# Revit family: Toilet-Elongated-American_Standard-Cadet_3_FloWise-3075000.020_Series
name_source: partatom
category: Plumbing Fixtures
units: mm (PartAtom-declared; Revit-internal decimal feet)

## family parameters
Always vertical = No
Cut with Voids When Loaded = No
OmniClass Number = 23.45.05.21.11
OmniClass Title = Water Closets
Part Type = Normal
Room Calculation Point = No
Round Connector Dimension = Use Radius
Shared = Yes
Work Plane-Based = Yes

## types (2) — shared parameters
3075.000 Right Height® Elongated Bowl with Seat = No
4000.101 Tank = No
4000.813 Tank with right hand trip lever = No
5024A.65G Preferred Seat Transitional Elongated Luxury Seat = No
ADA Compliant = Yes
Assembly Code = D2010110
Bowl Shape = Elongated
CW Connection = Yes
CWFU = 10
Cold Water Connection Diameter = 1/2"
Cold Water Connection Height = 5 1/2"
Cold Water Connection Width = 2 1/4"
Compliance Certifications = Meets or Exceeds the Following Specifications: • ASME A112.19.2/CSA B45.1-08 for Vitreous China Fixtures • US EPA WaterSense® Specification for HET's
Default Elevation = 0"
Description = Cadet® 3 FloWise® Skirted Chair Height Elongated Bowl With Seat
Finish = Vitreous China-American Standard-020-White
Finish - Trip Lever = Metal-American Standard-Chrome
Flush Rate = (4.8 Lpf/1.28 gpf)
HW Connection = No
Height = 30 3/4"
Inlet Position 1 = Yes
Inlet Position 2 = No
Inlet Position Distance = 2 1/4"
Installation Type = Floor Mounted
Length = 30 1/4"
Manufacturer = American Standard
Material = Vitreous China-American Standard-White
Model = 3075000.020
Product Documentation Link = https://lixil.cdn.celum.cloud
Product Page URL = https://www.americanstandard-us.com
Seat Height = 16 1/2"
URL = http://www.americanstandard-us.com
Vent Connection = No
WFU = 10
Warranty Information = Lifetime warranty on chinaware, 5 year warranty on all mechanical parts, and 1 year warranty on seat
Waste Connection = Yes
Waste Connection Diameter = 2 1/8"
Width = 15 3/4"
zero-valued in all types: HWFU

## per-type parameters (varying)
| type | 2989.101 trip lever on Left hand side | 2989.813 Same as above except with trip lever on right hand side | Left Trip Lever | Right Trip Lever |
| 3075000.020-2989.101 | No | Yes | No | Yes |
| 3075000.020-2989.813 | Yes | No | Yes | No |

## geometry (parser evidence)
native form markers: Sweep x3
no freeform markers — native parametric forms only
